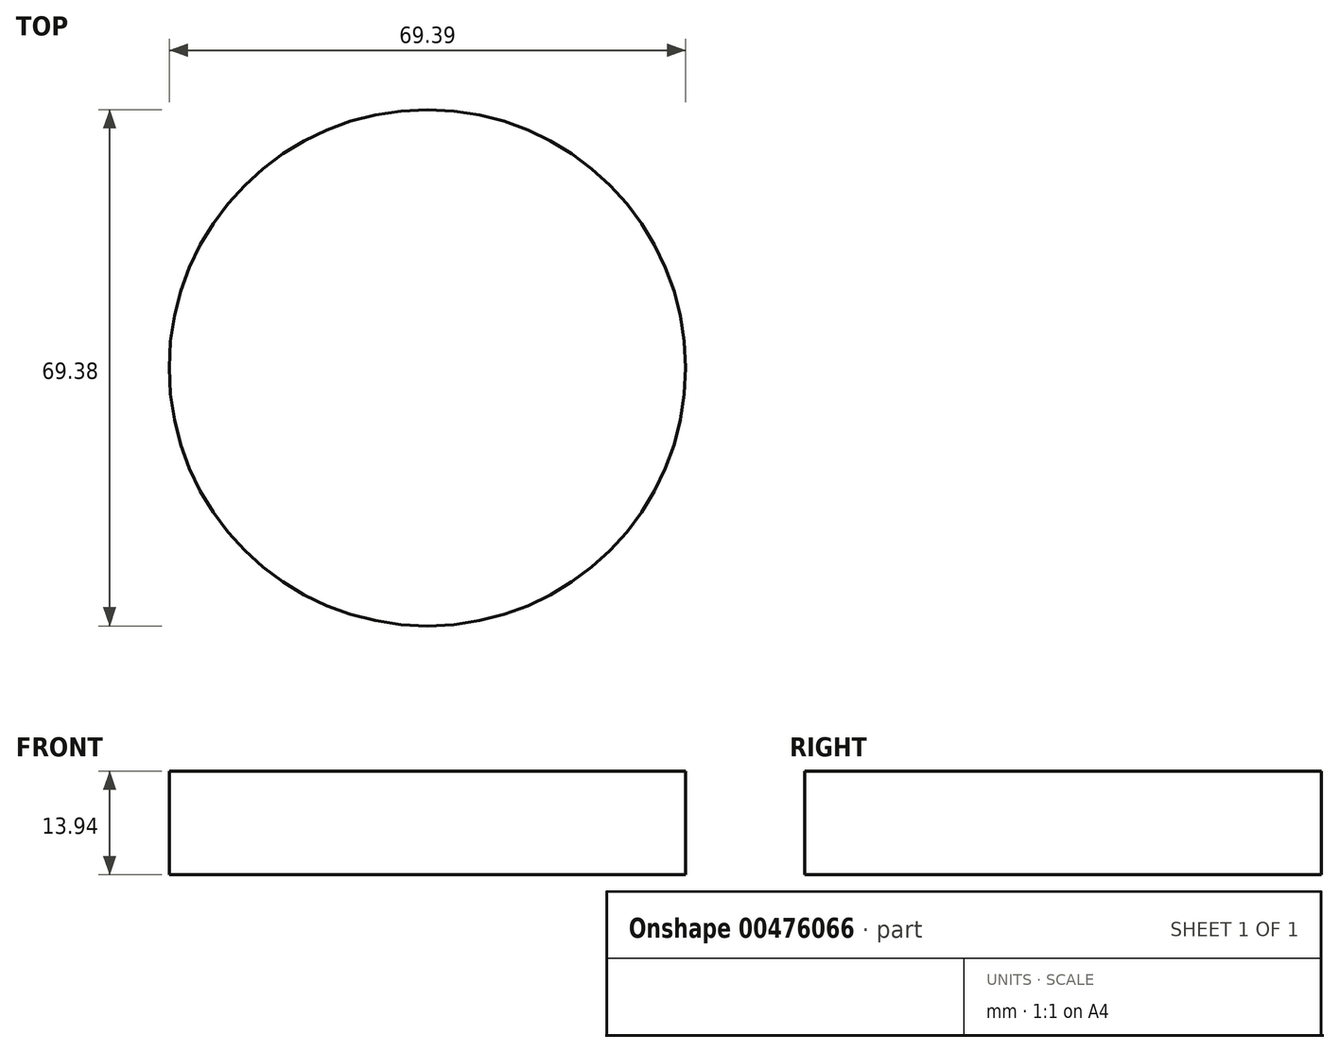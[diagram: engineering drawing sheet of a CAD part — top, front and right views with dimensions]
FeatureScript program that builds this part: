
annotation { "Feature Type Name" : "Feature", "Feature Type Description" : "" }
export const myFeature = defineFeature(function(context is Context, id is Id, definition is map)
    precondition{}
    {
        {
            var Q0;
            Q0=qCreatedBy(makeId("Front.planeOp"),FACE);
            var sketch = newSketch(context, id + "F0", { "sketchPlane" : qUnion([Q0])});
            skLineSegment(sketch, "E0.bottom", {"start": v(-91.07, 41.65) * mm, "end": v(-56.38, 41.65) * mm});
            skLineSegment(sketch, "E0.top", {"start": v(-91.07, 27.71) * mm, "end": v(-56.38, 27.71) * mm});
            skLineSegment(sketch, "E0.left", {"start": v(-91.07, 41.65) * mm, "end": v(-91.07, 27.71) * mm});
            skLineSegment(sketch, "E0.right", {"start": v(-56.38, 41.65) * mm, "end": v(-56.38, 27.71) * mm});
            skSolve(sketch);
        }
        {
            var Q0;
            Q0=makeQuery(id+"F0.imprint","IMPRINT",FACE,{"disambiguationData":[TD([[makeQuery(id+"F0.imprint","IMPRINT",EDGE,{"derivedFrom":sQuery(id+"F0.wireOp",EDGE,"E0.bottom")}),-1.0]])]});
            var Q1;
            Q1=sQuery(id+"F0.wireOp",EDGE,"E0.right");
            revolve(context, id + "F1", {"entities" : qUnion([Q0]), "axis" : qUnion([Q1]), "revolveType" : RevolveType.FULL});
        }
    });
